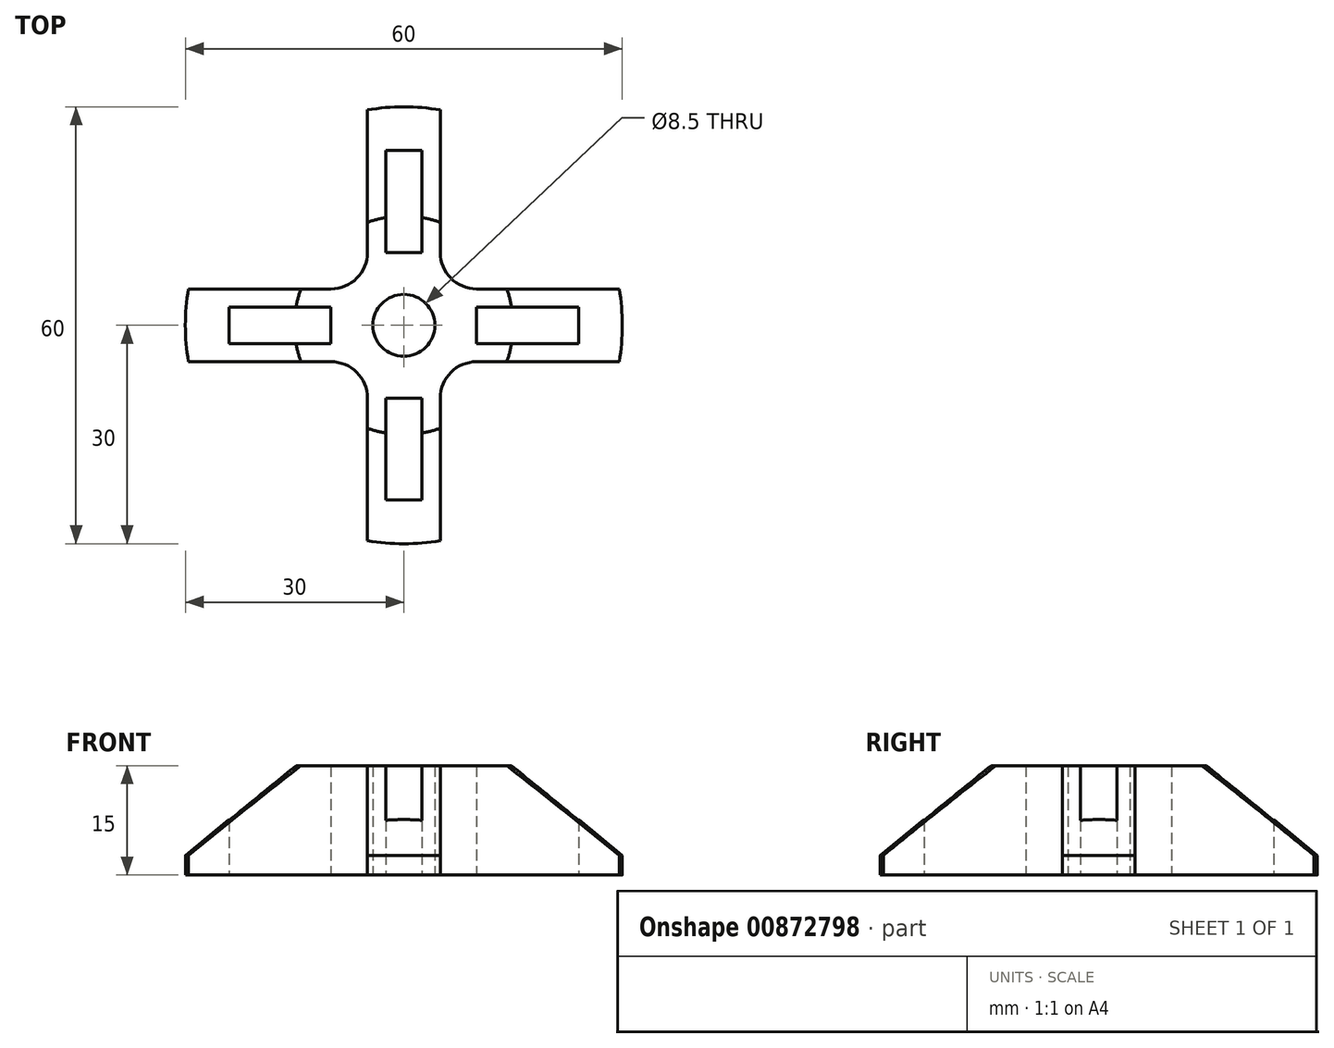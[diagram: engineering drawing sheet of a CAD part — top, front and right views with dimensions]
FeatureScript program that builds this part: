
annotation { "Feature Type Name" : "Feature", "Feature Type Description" : "" }
export const myFeature = defineFeature(function(context is Context, id is Id, definition is map)
    precondition{}
    {
        {
            assignVariable(context, id + "F0", {"name" : "Alto", "anyValue" : 15});
        }
        {
            var Q0;
            Q0=qCreatedBy(makeId("Top.planeOp"),FACE);
            var sketch = newSketch(context, id + "F1", { "sketchPlane" : qUnion([Q0])});
            skCircle(sketch, "E0", {"center": v(0, 0) * mm, "radius": 4.25 * mm});
            skCircle(sketch, "E1", {"center": v(0, 0) * mm, "radius": 30 * mm});
            skCircle(sketch, "E2", {"center": v(0, 0) * mm, "radius": 26.5 * mm});
            skLineSegment(sketch, "E3.bottom", {"start": v(-5, 42.51) * mm, "end": v(5, 42.51) * mm});
            skLineSegment(sketch, "E3.top", {"start": v(-5, -42.51) * mm, "end": v(5, -42.51) * mm});
            skLineSegment(sketch, "E3.left", {"start": v(-5, 42.51) * mm, "end": v(-5, -42.51) * mm});
            skLineSegment(sketch, "E3.right", {"start": v(5, 42.51) * mm, "end": v(5, -42.51) * mm});
            skLineSegment(sketch, "E4.bottom", {"start": v(-44.3, -5) * mm, "end": v(44.3, -5) * mm});
            skLineSegment(sketch, "E4.top", {"start": v(-44.3, 5) * mm, "end": v(44.3, 5) * mm});
            skLineSegment(sketch, "E4.left", {"start": v(-44.3, -5) * mm, "end": v(-44.3, 5) * mm});
            skLineSegment(sketch, "E4.right", {"start": v(44.3, -5) * mm, "end": v(44.3, 5) * mm});
            skLineSegment(sketch, "E5.bottom", {"start": v(10, -10) * mm, "end": v(-10, -10) * mm});
            skLineSegment(sketch, "E5.top", {"start": v(10, 10) * mm, "end": v(-10, 10) * mm});
            skLineSegment(sketch, "E5.left", {"start": v(10, -10) * mm, "end": v(10, 10) * mm});
            skLineSegment(sketch, "E5.right", {"start": v(-10, -10) * mm, "end": v(-10, 10) * mm});
            skLineSegment(sketch, "E6.bottom", {"start": v(24, -2.5) * mm, "end": v(-24, -2.5) * mm});
            skLineSegment(sketch, "E6.top", {"start": v(24, 2.5) * mm, "end": v(-24, 2.5) * mm});
            skLineSegment(sketch, "E6.left", {"start": v(24, -2.5) * mm, "end": v(24, 2.5) * mm});
            skLineSegment(sketch, "E6.right", {"start": v(-24, -2.5) * mm, "end": v(-24, 2.5) * mm});
            skLineSegment(sketch, "E7.bottom", {"start": v(-2.5, 24) * mm, "end": v(2.5, 24) * mm});
            skLineSegment(sketch, "E7.top", {"start": v(-2.5, -24) * mm, "end": v(2.5, -24) * mm});
            skLineSegment(sketch, "E7.left", {"start": v(-2.5, 24) * mm, "end": v(-2.5, -24) * mm});
            skLineSegment(sketch, "E7.right", {"start": v(2.5, 24) * mm, "end": v(2.5, -24) * mm});
            skSolve(sketch);
        }
        {
            var Q0;
            {var subQ0=sQuery(id+"F1.wireOp",EDGE,"E4.top");var subQ1=sQuery(id+"F1.wireOp",EDGE,"E1");var subQ2=makeQuery(id+"F1.imprint","INTERSECT",VERTEX,{"disambiguationData":[OD(1.0)],"derivedFrom":[subQ1,subQ0]});Q0=makeQuery(id+"F1.imprint","IMPRINT",FACE,{"disambiguationData":[TD([[makeQuery(id+"F1.imprint","IMPRINT",EDGE,{"disambiguationData":[TD([[subQ2,-1.0]])],"derivedFrom":subQ1}),1.0]])]});}
            var Q1;
            {var subQ0=sQuery(id+"F1.wireOp",EDGE,"E4.top");var subQ1=sQuery(id+"F1.wireOp",EDGE,"E2");var subQ2=makeQuery(id+"F1.imprint","INTERSECT",VERTEX,{"disambiguationData":[OD(1.0)],"derivedFrom":[subQ1,subQ0]});Q1=makeQuery(id+"F1.imprint","IMPRINT",FACE,{"disambiguationData":[TD([[makeQuery(id+"F1.imprint","IMPRINT",EDGE,{"disambiguationData":[TD([[subQ2,-1.0]])],"derivedFrom":subQ1}),1.0]])]});}
            var Q2;
            {var subQ0=sQuery(id+"F1.wireOp",EDGE,"E3.left");var subQ1=sQuery(id+"F1.wireOp",EDGE,"E2");var subQ2=makeQuery(id+"F1.imprint","INTERSECT",VERTEX,{"disambiguationData":[OD(1.0)],"derivedFrom":[subQ1,subQ0]});Q2=makeQuery(id+"F1.imprint","IMPRINT",FACE,{"disambiguationData":[TD([[makeQuery(id+"F1.imprint","IMPRINT",EDGE,{"disambiguationData":[TD([[subQ2,-1.0]])],"derivedFrom":subQ1}),1.0]])]});}
            var Q3;
            {var subQ0=sQuery(id+"F1.wireOp",EDGE,"E4.top");var subQ1=sQuery(id+"F1.wireOp",EDGE,"E2");var subQ2=makeQuery(id+"F1.imprint","INTERSECT",VERTEX,{"disambiguationData":[OD(0.0)],"derivedFrom":[subQ1,subQ0]});Q3=makeQuery(id+"F1.imprint","IMPRINT",FACE,{"disambiguationData":[TD([[makeQuery(id+"F1.imprint","IMPRINT",EDGE,{"disambiguationData":[TD([[subQ2,1.0]])],"derivedFrom":subQ1}),1.0]])]});}
            var Q4;
            {var subQ0=sQuery(id+"F1.wireOp",EDGE,"E3.right");var subQ1=sQuery(id+"F1.wireOp",EDGE,"E2");var subQ2=makeQuery(id+"F1.imprint","INTERSECT",VERTEX,{"disambiguationData":[OD(0.0)],"derivedFrom":[subQ1,subQ0]});Q4=makeQuery(id+"F1.imprint","IMPRINT",FACE,{"disambiguationData":[TD([[makeQuery(id+"F1.imprint","IMPRINT",EDGE,{"disambiguationData":[TD([[subQ2,-1.0]])],"derivedFrom":subQ1}),1.0]])]});}
            var Q5;
            {var subQ0=sQuery(id+"F1.wireOp",EDGE,"E3.right");var subQ1=sQuery(id+"F1.wireOp",EDGE,"E1");var subQ2=makeQuery(id+"F1.imprint","INTERSECT",VERTEX,{"disambiguationData":[OD(0.0)],"derivedFrom":[subQ1,subQ0]});Q5=makeQuery(id+"F1.imprint","IMPRINT",FACE,{"disambiguationData":[TD([[makeQuery(id+"F1.imprint","IMPRINT",EDGE,{"disambiguationData":[TD([[subQ2,-1.0]])],"derivedFrom":subQ1}),1.0]])]});}
            var Q6;
            {var subQ0=sQuery(id+"F1.wireOp",EDGE,"E4.top");var subQ1=sQuery(id+"F1.wireOp",EDGE,"E1");var subQ2=makeQuery(id+"F1.imprint","INTERSECT",VERTEX,{"disambiguationData":[OD(0.0)],"derivedFrom":[subQ1,subQ0]});Q6=makeQuery(id+"F1.imprint","IMPRINT",FACE,{"disambiguationData":[TD([[makeQuery(id+"F1.imprint","IMPRINT",EDGE,{"disambiguationData":[TD([[subQ2,1.0]])],"derivedFrom":subQ1}),1.0]])]});}
            var Q7;
            Q7=makeQuery(id+"F1.imprint","IMPRINT",FACE,{"disambiguationData":[TD([[makeQuery(id+"F1.imprint","IMPRINT",EDGE,{"derivedFrom":sQuery(id+"F1.wireOp",EDGE,"E0")}),-1.0]])]});
            var Q8;
            {var subQ0=sQuery(id+"F1.wireOp",EDGE,"E3.left");var subQ1=sQuery(id+"F1.wireOp",EDGE,"E1");var subQ2=makeQuery(id+"F1.imprint","INTERSECT",VERTEX,{"disambiguationData":[OD(1.0)],"derivedFrom":[subQ1,subQ0]});Q8=makeQuery(id+"F1.imprint","IMPRINT",FACE,{"disambiguationData":[TD([[makeQuery(id+"F1.imprint","IMPRINT",EDGE,{"disambiguationData":[TD([[subQ2,-1.0]])],"derivedFrom":subQ1}),1.0]])]});}
            var Q9;
            {var subQ0=sQuery(id+"F1.wireOp",EDGE,"E4.top");var subQ1=sQuery(id+"F1.wireOp",EDGE,"E3.left");var subQ2=makeQuery(id+"F1.imprint","INTERSECT",VERTEX,{"derivedFrom":[subQ1,subQ0]});Q9=makeQuery(id+"F1.imprint","IMPRINT",FACE,{"disambiguationData":[TD([[makeQuery(id+"F1.imprint","IMPRINT",EDGE,{"disambiguationData":[TD([[subQ2,-1.0]])],"derivedFrom":subQ1}),-1.0]])]});}
            var Q10;
            {var subQ3=sQuery(id+"F1.wireOp",EDGE,"E7.left");var subQ7=sQuery(id+"F1.wireOp",EDGE,"E0");var subQ9=makeQuery(id+"F1.imprint","INTERSECT",VERTEX,{"disambiguationData":[OD(0.0)],"derivedFrom":[subQ7,subQ3]});Q10=makeQuery(id+"F1.imprint","IMPRINT",FACE,{"disambiguationData":[TD([[makeQuery(id+"F1.imprint","IMPRINT",EDGE,{"disambiguationData":[TD([[subQ9,-1.0]])],"derivedFrom":subQ7}),-1.0]])]});}
            var Q11;
            {var subQ1=sQuery(id+"F1.wireOp",EDGE,"E0");var subQ5=sQuery(id+"F1.wireOp",EDGE,"E7.right");var subQ6=makeQuery(id+"F1.imprint","INTERSECT",VERTEX,{"disambiguationData":[OD(0.0)],"derivedFrom":[subQ1,subQ5]});Q11=makeQuery(id+"F1.imprint","IMPRINT",FACE,{"disambiguationData":[TD([[makeQuery(id+"F1.imprint","IMPRINT",EDGE,{"disambiguationData":[TD([[subQ6,1.0]])],"derivedFrom":subQ1}),-1.0]])]});}
            var Q12;
            {var subQ0=sQuery(id+"F1.wireOp",EDGE,"E4.top");var subQ1=sQuery(id+"F1.wireOp",EDGE,"E3.right");var subQ2=makeQuery(id+"F1.imprint","INTERSECT",VERTEX,{"derivedFrom":[subQ1,subQ0]});Q12=makeQuery(id+"F1.imprint","IMPRINT",FACE,{"disambiguationData":[TD([[makeQuery(id+"F1.imprint","IMPRINT",EDGE,{"disambiguationData":[TD([[subQ2,-1.0]])],"derivedFrom":subQ1}),1.0]])]});}
            var Q13;
            {var subQ0=sQuery(id+"F1.wireOp",EDGE,"E4.bottom");var subQ1=sQuery(id+"F1.wireOp",EDGE,"E3.right");var subQ2=makeQuery(id+"F1.imprint","INTERSECT",VERTEX,{"derivedFrom":[subQ1,subQ0]});Q13=makeQuery(id+"F1.imprint","IMPRINT",FACE,{"disambiguationData":[TD([[makeQuery(id+"F1.imprint","IMPRINT",EDGE,{"disambiguationData":[TD([[subQ2,-1.0]])],"derivedFrom":subQ1}),-1.0]])]});}
            var Q14;
            {var subQ0=sQuery(id+"F1.wireOp",EDGE,"E7.left");var subQ1=sQuery(id+"F1.wireOp",EDGE,"E4.bottom");var subQ2=makeQuery(id+"F1.imprint","INTERSECT",VERTEX,{"derivedFrom":[subQ1,subQ0]});Q14=makeQuery(id+"F1.imprint","IMPRINT",FACE,{"disambiguationData":[TD([[makeQuery(id+"F1.imprint","IMPRINT",EDGE,{"disambiguationData":[TD([[subQ2,-1.0]])],"derivedFrom":subQ1}),-1.0]])]});}
            var Q15;
            {var subQ0=sQuery(id+"F1.wireOp",EDGE,"E4.bottom");var subQ1=sQuery(id+"F1.wireOp",EDGE,"E3.left");var subQ2=makeQuery(id+"F1.imprint","INTERSECT",VERTEX,{"derivedFrom":[subQ1,subQ0]});Q15=makeQuery(id+"F1.imprint","IMPRINT",FACE,{"disambiguationData":[TD([[makeQuery(id+"F1.imprint","IMPRINT",EDGE,{"disambiguationData":[TD([[subQ2,-1.0]])],"derivedFrom":subQ1}),1.0]])]});}
            var Q16;
            {var subQ1=sQuery(id+"F1.wireOp",EDGE,"E0");var subQ5=sQuery(id+"F1.wireOp",EDGE,"E7.right");var subQ6=makeQuery(id+"F1.imprint","INTERSECT",VERTEX,{"disambiguationData":[OD(1.0)],"derivedFrom":[subQ1,subQ5]});Q16=makeQuery(id+"F1.imprint","IMPRINT",FACE,{"disambiguationData":[TD([[makeQuery(id+"F1.imprint","IMPRINT",EDGE,{"disambiguationData":[TD([[subQ6,-1.0]])],"derivedFrom":subQ1}),-1.0]])]});}
            var Q17;
            {var subQ0=sQuery(id+"F1.wireOp",EDGE,"E6.bottom");var subQ1=sQuery(id+"F1.wireOp",EDGE,"E0");var subQ2=makeQuery(id+"F1.imprint","INTERSECT",VERTEX,{"disambiguationData":[OD(0.0)],"derivedFrom":[subQ1,subQ0]});Q17=makeQuery(id+"F1.imprint","IMPRINT",FACE,{"disambiguationData":[TD([[makeQuery(id+"F1.imprint","IMPRINT",EDGE,{"disambiguationData":[TD([[subQ2,-1.0]])],"derivedFrom":subQ1}),-1.0]])]});}
            var Q18;
            {var subQ0=sQuery(id+"F1.wireOp",EDGE,"E6.bottom");var subQ1=sQuery(id+"F1.wireOp",EDGE,"E3.left");var subQ2=makeQuery(id+"F1.imprint","INTERSECT",VERTEX,{"derivedFrom":[subQ1,subQ0]});Q18=makeQuery(id+"F1.imprint","IMPRINT",FACE,{"disambiguationData":[TD([[makeQuery(id+"F1.imprint","IMPRINT",EDGE,{"disambiguationData":[TD([[subQ2,-1.0]])],"derivedFrom":subQ1}),-1.0]])]});}
            var Q19;
            {var subQ0=sQuery(id+"F1.wireOp",EDGE,"E6.bottom");var subQ1=sQuery(id+"F1.wireOp",EDGE,"E3.right");var subQ2=makeQuery(id+"F1.imprint","INTERSECT",VERTEX,{"derivedFrom":[subQ1,subQ0]});Q19=makeQuery(id+"F1.imprint","IMPRINT",FACE,{"disambiguationData":[TD([[makeQuery(id+"F1.imprint","IMPRINT",EDGE,{"disambiguationData":[TD([[subQ2,-1.0]])],"derivedFrom":subQ1}),1.0]])]});}
            var Q20;
            {var subQ0=sQuery(id+"F1.wireOp",EDGE,"E5.top");var subQ1=sQuery(id+"F1.wireOp",EDGE,"E3.right");var subQ2=makeQuery(id+"F1.imprint","INTERSECT",VERTEX,{"derivedFrom":[subQ1,subQ0]});Q20=makeQuery(id+"F1.imprint","IMPRINT",FACE,{"disambiguationData":[TD([[makeQuery(id+"F1.imprint","IMPRINT",EDGE,{"disambiguationData":[TD([[subQ2,-1.0]])],"derivedFrom":subQ1}),-1.0]])]});}
            var Q21;
            {var subQ0=sQuery(id+"F1.wireOp",EDGE,"E7.left");var subQ1=sQuery(id+"F1.wireOp",EDGE,"E4.top");var subQ2=makeQuery(id+"F1.imprint","INTERSECT",VERTEX,{"derivedFrom":[subQ1,subQ0]});Q21=makeQuery(id+"F1.imprint","IMPRINT",FACE,{"disambiguationData":[TD([[makeQuery(id+"F1.imprint","IMPRINT",EDGE,{"disambiguationData":[TD([[subQ2,-1.0]])],"derivedFrom":subQ1}),1.0]])]});}
            var Q22;
            {var subQ0=sQuery(id+"F1.wireOp",EDGE,"E6.top");var subQ1=sQuery(id+"F1.wireOp",EDGE,"E3.left");var subQ2=makeQuery(id+"F1.imprint","INTERSECT",VERTEX,{"derivedFrom":[subQ1,subQ0]});Q22=makeQuery(id+"F1.imprint","IMPRINT",FACE,{"disambiguationData":[TD([[makeQuery(id+"F1.imprint","IMPRINT",EDGE,{"disambiguationData":[TD([[subQ2,-1.0]])],"derivedFrom":subQ1}),-1.0]])]});}
            var Q23;
            {var subQ0=sQuery(id+"F1.wireOp",EDGE,"E6.top");var subQ1=sQuery(id+"F1.wireOp",EDGE,"E3.right");var subQ2=makeQuery(id+"F1.imprint","INTERSECT",VERTEX,{"derivedFrom":[subQ1,subQ0]});Q23=makeQuery(id+"F1.imprint","IMPRINT",FACE,{"disambiguationData":[TD([[makeQuery(id+"F1.imprint","IMPRINT",EDGE,{"disambiguationData":[TD([[subQ2,-1.0]])],"derivedFrom":subQ1}),1.0]])]});}
            var Q24;
            {var subQ0=sQuery(id+"F1.wireOp",EDGE,"E5.top");var subQ1=sQuery(id+"F1.wireOp",EDGE,"E3.left");var subQ2=makeQuery(id+"F1.imprint","INTERSECT",VERTEX,{"derivedFrom":[subQ1,subQ0]});Q24=makeQuery(id+"F1.imprint","IMPRINT",FACE,{"disambiguationData":[TD([[makeQuery(id+"F1.imprint","IMPRINT",EDGE,{"disambiguationData":[TD([[subQ2,-1.0]])],"derivedFrom":subQ1}),1.0]])]});}
            extrude(context, id + "F2", {"entities" : qUnion([Q0, Q1, Q2, Q3, Q4, Q5, Q6, Q7, Q8, Q9, Q10, Q11, Q12, Q13, Q14, Q15, Q16, Q17, Q18, Q19, Q20, Q21, Q22, Q23, Q24]), "depth" : (getVariable(context, 'Alto')) * mm, "offsetDistance" : 25 * mm});
        }
        {
            var Q0;
            Q0=qCreatedBy(makeId("Front.planeOp"),FACE);
            var sketch = newSketch(context, id + "F3", { "sketchPlane" : qUnion([Q0])});
            skLineSegment(sketch, "E8", {"start": v(0, 0) * mm, "end": v(-30, 0) * mm});
            skLineSegment(sketch, "E9", {"start": v(-30, 0) * mm, "end": v(-30, 2.7) * mm});
            skLineSegment(sketch, "E10", {"start": v(0, 0) * mm, "end": v(0, 15) * mm});
            skLineSegment(sketch, "E11", {"start": v(0, 15) * mm, "end": v(-15, 15) * mm});
            skLineSegment(sketch, "E12", {"start": v(-15, 15) * mm, "end": v(-30, 2.7) * mm});
            skLineSegment(sketch, "E13", {"start": v(-15, 15) * mm, "end": v(-30, 15) * mm});
            skLineSegment(sketch, "E14", {"start": v(-30, 15) * mm, "end": v(-30, 2.7) * mm});
            skSolve(sketch);
        }
        {
            var Q0;
            Q0=makeQuery(id+"F3.imprint","IMPRINT",FACE,{"disambiguationData":[TD([[makeQuery(id+"F3.imprint","IMPRINT",EDGE,{"derivedFrom":sQuery(id+"F3.wireOp",EDGE,"E12")}),-1.0]])]});
            var Q1;
            Q1=sQuery(id+"F3.wireOp",EDGE,"E10");
            revolve(context, id + "F4", {"operationType" : NewBodyOperationType.REMOVE, "surfaceOperationType" : NewSurfaceOperationType.NEW, "entities" : qUnion([Q0]), "axis" : qUnion([Q1]), "revolveType" : RevolveType.FULL, "oppositeDirection" : true});
        }
        {
            var Q0;
            Q0=makeQuery(id+"F2.opExtrude","SWEPT_EDGE",EDGE,{"disambiguationData":[OSD([sQuery(id+"F1.wireOp",EDGE,"E3.right"),sQuery(id+"F1.wireOp",EDGE,"E4.top")])]});
            var Q1;
            Q1=makeQuery(id+"F2.opExtrude","SWEPT_EDGE",EDGE,{"disambiguationData":[OSD([sQuery(id+"F1.wireOp",EDGE,"E3.right"),sQuery(id+"F1.wireOp",EDGE,"E4.bottom")])]});
            var Q2;
            Q2=makeQuery(id+"F2.opExtrude","SWEPT_EDGE",EDGE,{"disambiguationData":[OSD([sQuery(id+"F1.wireOp",EDGE,"E3.left"),sQuery(id+"F1.wireOp",EDGE,"E4.bottom")])]});
            var Q3;
            Q3=makeQuery(id+"F2.opExtrude","SWEPT_EDGE",EDGE,{"disambiguationData":[OSD([sQuery(id+"F1.wireOp",EDGE,"E3.left"),sQuery(id+"F1.wireOp",EDGE,"E4.top")])]});
            fillet(context, id + "F5", {"entities" : qUnion([Q0, Q1, Q2, Q3]), "radius" : 5 * mm, "tangentPropagation" : true, "allowEdgeOverflow" : false});
        }
    });
